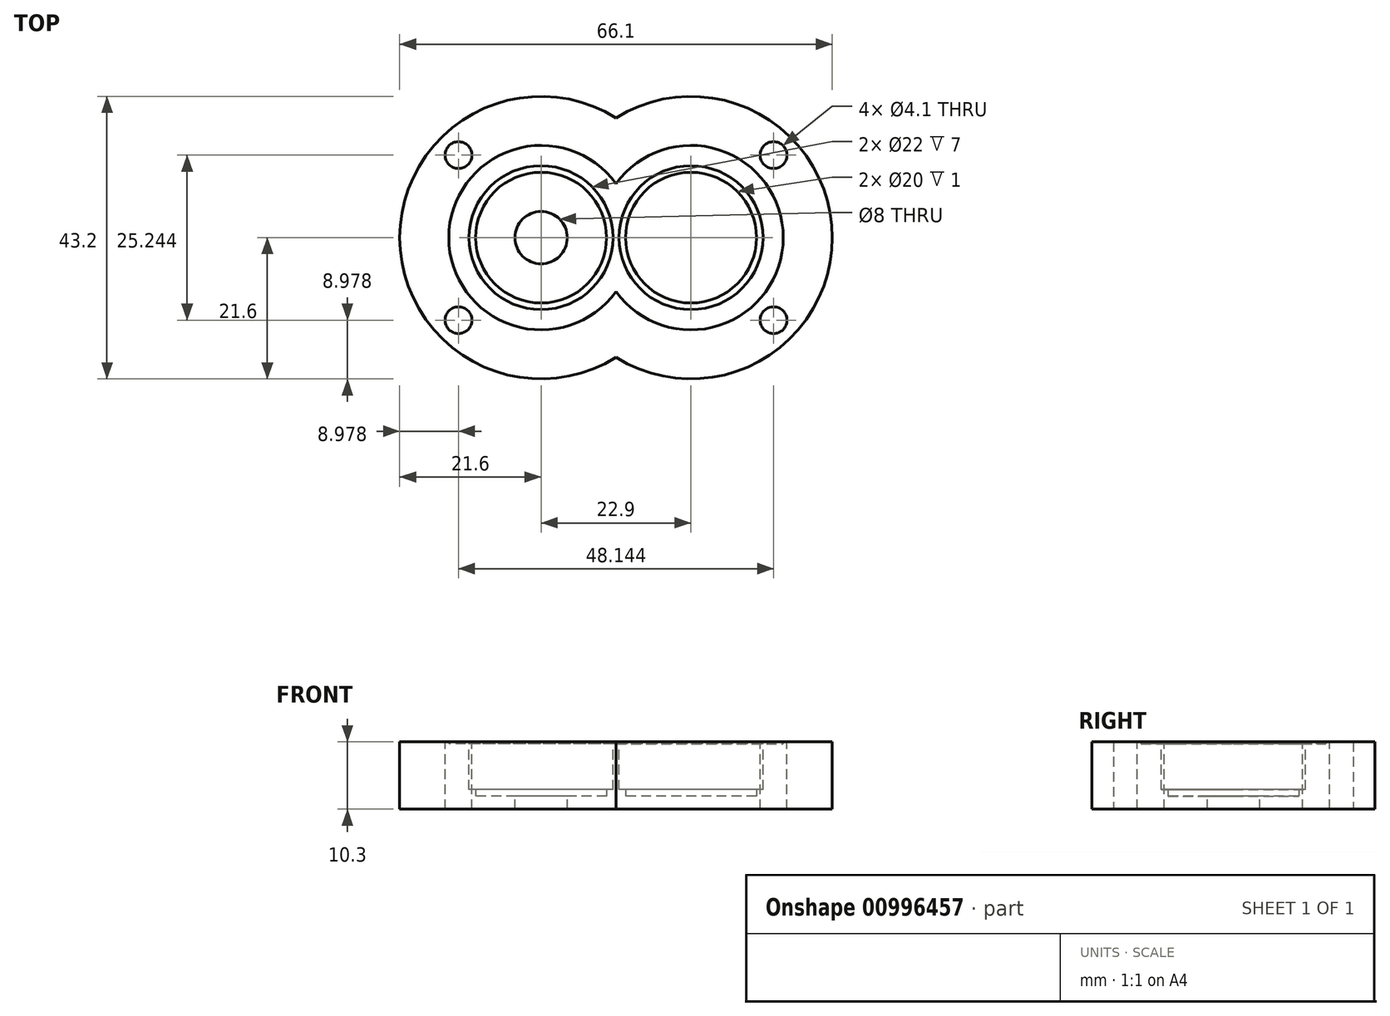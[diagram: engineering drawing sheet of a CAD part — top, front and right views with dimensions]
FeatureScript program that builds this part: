
annotation { "Feature Type Name" : "Feature", "Feature Type Description" : "" }
export const myFeature = defineFeature(function(context is Context, id is Id, definition is map)
    precondition{}
    {
        {
            var Q0;
            Q0=qCreatedBy(makeId("Top.planeOp"),FACE);
            var sketch = newSketch(context, id + "F0", { "sketchPlane" : qUnion([Q0])});
            skArc(sketch, "E0", {"start": v(0, 8.23) * mm, "mid": v(-25.55, 0) * mm, "end": v(0, -8.23) * mm});
            skLineSegment(sketch, "E1", {"start": v(-11.45, 0) * mm, "end": v(11.45, 0) * mm, "construction": true});
            skLineSegment(sketch, "E2", {"start": v(0, 0) * mm, "end": v(0, 8.23) * mm, "construction": true});
            skArc(sketch, "E3.0", {"start": v(0, 18.32) * mm, "mid": v(-33.05, 0) * mm, "end": v(0, -18.32) * mm});
            skLineSegment(sketch, "E4", {"start": v(0, -18.32) * mm, "end": v(0, 18.32) * mm, "construction": true});
            skArc(sketch, "E5.MirrorCS", {"start": v(0, 8.23) * mm, "mid": v(25.55, 0) * mm, "end": v(0, -8.23) * mm});
            skArc(sketch, "E6.MirrorCS", {"start": v(0, 18.32) * mm, "mid": v(33.05, 0) * mm, "end": v(0, -18.32) * mm});
            skSolve(sketch);
        }
        {
            var Q0;
            Q0=qSketchRegion(id+"F0",true);
            extrude(context, id + "F1", {"entities" : qUnion([Q0]), "depth" : 0.3 * mm, "offsetDistance" : 25 * mm});
        }
        {
            var Q0;
            Q0=makeQuery(id+"F1.opExtrude","CAP_FACE",FACE,{"disambiguationData":[OSD([sQuery(id+"F0.wireOp",EDGE,"E0"),sQuery(id+"F0.wireOp",EDGE,"E3.0"),sQuery(id+"F0.wireOp",EDGE,"E5.MirrorCS"),sQuery(id+"F0.wireOp",EDGE,"E6.MirrorCS")])],"isStart":true});
            var sketch = newSketch(context, id + "F2", { "sketchPlane" : qUnion([Q0])});
            skArc(sketch, "E7.0", {"start": v(0, -18.32) * mm, "mid": v(33.05, 0) * mm, "end": v(0, 18.32) * mm});
            skArc(sketch, "E8.0", {"start": v(0, -18.32) * mm, "mid": v(-33.05, 0) * mm, "end": v(0, 18.32) * mm});
            skSolve(sketch);
        }
        {
            var Q0;
            Q0=qSketchRegion(id+"F2",true);
            extrude(context, id + "F3", {"entities" : qUnion([Q0]), "operationType" : NewBodyOperationType.ADD, "depth" : 10 * mm, "offsetDistance" : 25 * mm});
        }
        {
            var Q0;
            Q0=makeQuery(id+"F3.opExtrude","CAP_FACE",FACE,{"disambiguationData":[OSD([sQuery(id+"F2.wireOp",EDGE,"E7.0"),sQuery(id+"F2.wireOp",EDGE,"E8.0")])],"isStart":true});
            var sketch = newSketch(context, id + "F4", { "sketchPlane" : qUnion([Q0])});
            skArc(sketch, "E9.0", {"start": v(0, 8.23) * mm, "mid": v(25.55, 0) * mm, "end": v(0, -8.23) * mm, "construction": true});
            skArc(sketch, "E10.0", {"start": v(0, 8.23) * mm, "mid": v(-25.55, 0) * mm, "end": v(0, -8.23) * mm, "construction": true});
            skCircle(sketch, "E11", {"center": v(-11.45, 0) * mm, "radius": 11 * mm});
            skCircle(sketch, "E12", {"center": v(11.45, 0) * mm, "radius": 11 * mm});
            skSolve(sketch);
        }
        {
            var Q0;
            Q0=qSketchRegion(id+"F4",true);
            extrude(context, id + "F5", {"entities" : qUnion([Q0]), "operationType" : NewBodyOperationType.REMOVE, "oppositeDirection" : true, "depth" : 8 * mm, "offsetDistance" : 25 * mm});
        }
        {
            var Q0;
            Q0=makeQuery(id+"F5.boolean.opBoolean","COPY",FACE,{"derivedFrom":makeQuery(id+"F5.opExtrude","CAP_FACE",FACE,{"disambiguationData":[OSD([sQuery(id+"F4.wireOp",EDGE,"E11")])],"isStart":false})});
            var sketch = newSketch(context, id + "F6", { "sketchPlane" : qUnion([Q0])});
            skCircle(sketch, "E13.0", {"center": v(-11.45, 0) * mm, "radius": 11 * mm});
            skCircle(sketch, "E14.0", {"center": v(11.45, 0) * mm, "radius": 11 * mm});
            skCircle(sketch, "E15.0", {"center": v(-11.45, 0) * mm, "radius": 10 * mm});
            skCircle(sketch, "E16.0", {"center": v(11.45, 0) * mm, "radius": 10 * mm});
            skSolve(sketch);
        }
        {
            var Q0;
            Q0=qSketchRegion(id+"F6",true);
            extrude(context, id + "F7", {"entities" : qUnion([Q0]), "operationType" : NewBodyOperationType.ADD, "depth" : 1 * mm, "offsetDistance" : 25 * mm});
        }
        {
            var Q0;
            Q0=makeQuery(id+"F5.boolean.opBoolean","COPY",FACE,{"derivedFrom":makeQuery(id+"F5.opExtrude","CAP_FACE",FACE,{"disambiguationData":[OSD([sQuery(id+"F4.wireOp",EDGE,"E11")])],"isStart":false})});
            var sketch = newSketch(context, id + "F8", { "sketchPlane" : qUnion([Q0])});
            skCircle(sketch, "E17", {"center": v(-11.45, 0) * mm, "radius": 4 * mm});
            skSolve(sketch);
        }
        {
            var Q0;
            Q0=qSketchRegion(id+"F8",true);
            extrude(context, id + "F9", {"entities" : qUnion([Q0]), "operationType" : NewBodyOperationType.REMOVE, "endBound" : BoundingType.THROUGH_ALL, "oppositeDirection" : true, "depth" : 25 * mm, "offsetDistance" : 25 * mm});
        }
        {
            var Q0;
            Q0=makeQuery(id+"F1.opExtrude","CAP_FACE",FACE,{"disambiguationData":[OSD([sQuery(id+"F0.wireOp",EDGE,"E0"),sQuery(id+"F0.wireOp",EDGE,"E3.0"),sQuery(id+"F0.wireOp",EDGE,"E5.MirrorCS"),sQuery(id+"F0.wireOp",EDGE,"E6.MirrorCS")])],"isStart":false});
            var sketch = newSketch(context, id + "F10", { "sketchPlane" : qUnion([Q0])});
            skCircle(sketch, "E18", {"center": v(-24.07, 12.62) * mm, "radius": 2.05 * mm});
            skLineSegment(sketch, "E19", {"start": v(0, 18.32) * mm, "end": v(0, -18.32) * mm, "construction": true});
            skCircle(sketch, "E20.0", {"center": v(-11.45, 0) * mm, "radius": 4 * mm, "construction": true});
            skLineSegment(sketch, "E21", {"start": v(-11.45, 0) * mm, "end": v(-21.42, 9.97) * mm, "construction": true});
            skArc(sketch, "E22.0", {"start": v(0, 8.23) * mm, "mid": v(-25.55, 0) * mm, "end": v(0, -8.23) * mm, "construction": true});
            skLineSegment(sketch, "E23", {"start": v(-21.42, 9.97) * mm, "end": v(-24.07, 12.62) * mm, "construction": true});
            skLineSegment(sketch, "E24", {"start": v(-24.07, 12.62) * mm, "end": v(-26.72, 15.27) * mm, "construction": true});
            skLineSegment(sketch, "E25", {"start": v(-11.45, 0) * mm, "end": v(-25.55, 0) * mm, "construction": true});
            skCircle(sketch, "E26.MirrorC", {"center": v(-24.07, -12.62) * mm, "radius": 2.05 * mm});
            skCircle(sketch, "E27.MirrorC", {"center": v(24.07, 12.62) * mm, "radius": 2.05 * mm});
            skCircle(sketch, "E28.MirrorC", {"center": v(24.07, -12.62) * mm, "radius": 2.05 * mm});
            skSolve(sketch);
        }
        {
            var Q0;
            Q0=qSketchRegion(id+"F10",true);
            extrude(context, id + "F11", {"entities" : qUnion([Q0]), "operationType" : NewBodyOperationType.REMOVE, "endBound" : BoundingType.THROUGH_ALL, "oppositeDirection" : true, "depth" : 25 * mm, "offsetDistance" : 25 * mm});
        }
    });
